# Revit family: Franke_ChillandCup_CC05_EC-A600_MS_EC_A600_FM_EC_A800_FM_EC
name_source: partatom
category: Sonderausstattung
revit_build: Autodesk Revit 2015 (Build: 20140606_1530(x64)
units: mm (PartAtom-declared; Revit-internal decimal feet)

## types (1)
- ChillandCup CC05 EC-A600 MS EC,A600 FM EC,A800 FM EC(220-230V/EU)
    Anzahl der Nullleiter = 1
    Anzahl der Schutzleiter = 1
    Anzahl von Polen = 1
    Aufstellgewicht = 29 kg
    Bauelement = Tassenwärmer, Milchkühleinheit integriert
    Baugruppenkennzeichen = Tassenwärmer, Milchkühleinheit integriert
    Beschreibung = Tassenwärmer, 2 Ablagen beheizt, Milchkühleinheit integriert
    Breite = 320 mm  [stored 1.04987 ft]
    Energieverlust nach DIN18873 = 2.020 kWh/24 h - 230 V
    Hersteller = Franke
    Höhe = 582 mm  [stored 1.90945 ft]
    Kosten = 0 $
    Kühleinheit = 5 l
    Leistung = 170 W
    Modell = ChillandCup CC05 EC-A600 MS EC,A600 FM EC, A800 FM EC
    Netzfrequenz = 50 Hz
    Netzfrequenz alternativ = 60 Hz
    Sicherung = 16 A
    Spannung max. = 230 V
    Spannung min. = 220 V
    Tassenwärmereinheit = 80 Tassen
    Temperaturbereich = + 3° bis + 8°
    Tiefe = 489 mm  [stored 1.60433 ft]
    URL = https://www.franke.com

note: [stored X ft] marks values corroborated as IEEE doubles in the binary element streams (Revit-internal decimal feet)
